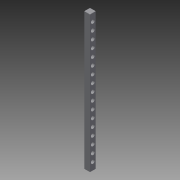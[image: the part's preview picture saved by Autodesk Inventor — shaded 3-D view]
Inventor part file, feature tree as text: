
AUTODESK INVENTOR PART (.ipt)
format: ipt  version: 2015 (Build 190159000, 159)  size: 112,128 bytes
history: native  units: in
note: dims shown in document units (in); Inventor stores cm internally (conversion verified against a paired STEP export)
features: extrude x2, sketch x2
ambient origin geometry x8: Origin, YZ Plane, XZ Plane, XY Plane, X Axis, Y Axis, Z Axis, Center Point
bodies: Solid1 (feature_tree)
feature tree (4):
  extrude  "Extrusion1"  Depth=3.0in
  extrude  "Extrusion2"  Depth=3.0in
  sketch  "Sketch1"  dims[d0=72.0in d1=3.0in]
  sketch  "Sketch2"  dims[d2=3.0in d3=0.0in d4=2.0in d5=2.0in d6=2.0in d7=2.0in d8=2.0in d9=2.0in d10=2.0in d11=2.0in d12=2.0in d13=2.0in d14=2.0in d15=2.0in d16=2.0in d17=2.0in d18=2.0in d19=2.0in d20=2.0in d21=5.0in d22=0.0in]
